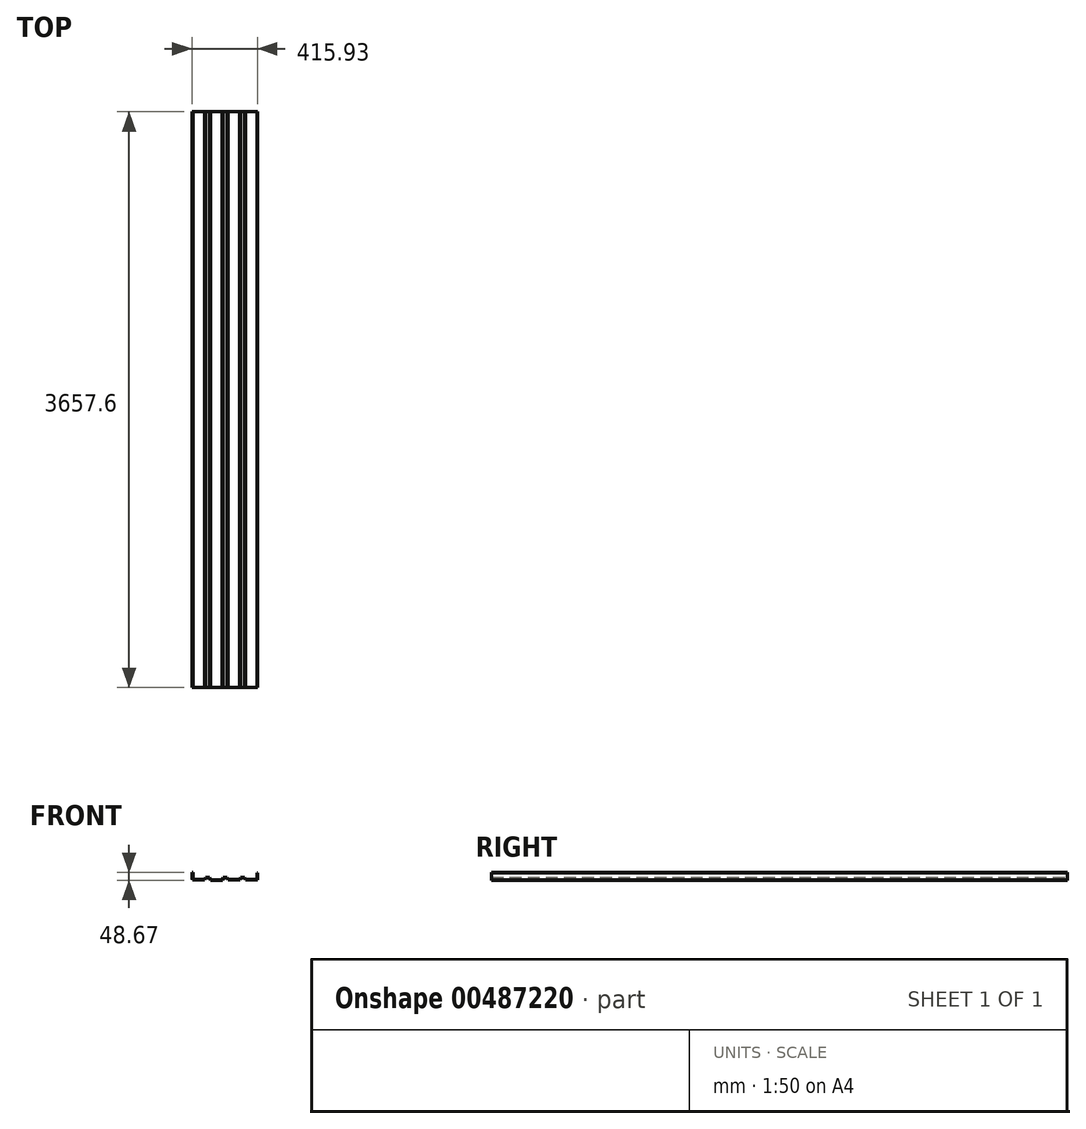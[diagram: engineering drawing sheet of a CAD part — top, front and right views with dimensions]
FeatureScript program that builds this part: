
annotation { "Feature Type Name" : "Feature", "Feature Type Description" : "" }
export const myFeature = defineFeature(function(context is Context, id is Id, definition is map)
    precondition{}
    {
        {
            var Q0;
            Q0=qCreatedBy(makeId("Front.planeOp"),FACE);
            var sketch = newSketch(context, id + "F0", { "sketchPlane" : qUnion([Q0])});
            skLineSegment(sketch, "E0.top", {"start": v(-11.38, 6.35) * mm, "end": v(14.02, 6.35) * mm});
            skPoint(sketch, "E0.middle", {"position": v(0, 0) * mm});
            skLineSegment(sketch, "E1.top", {"start": v(99.74, 6.35) * mm, "end": v(125.14, 6.35) * mm});
            skPoint(sketch, "E1.middle", {"position": v(111.12, 0) * mm});
            skLineSegment(sketch, "E2.top", {"start": v(-98.42, 6.35) * mm, "end": v(-123.83, 6.35) * mm});
            skPoint(sketch, "E2.middle", {"position": v(-111.12, 0) * mm});
            skLineSegment(sketch, "E3", {"start": v(-130.17, -6.35) * mm, "end": v(-123.83, 6.35) * mm});
            skLineSegment(sketch, "E4", {"start": v(-90.76, -8.98) * mm, "end": v(-98.42, 6.35) * mm});
            skLineSegment(sketch, "E5", {"start": v(-17.73, -8.98) * mm, "end": v(-11.38, 6.35) * mm});
            skLineSegment(sketch, "E6", {"start": v(20.37, -6.35) * mm, "end": v(14.02, 6.35) * mm});
            skLineSegment(sketch, "E7", {"start": v(93.4, -6.35) * mm, "end": v(99.74, 6.35) * mm});
            skLineSegment(sketch, "E8", {"start": v(131.5, -6.35) * mm, "end": v(125.14, 6.35) * mm});
            skLineSegment(sketch, "E9", {"start": v(-90.76, -8.98) * mm, "end": v(-17.73, -8.98) * mm});
            skLineSegment(sketch, "E10", {"start": v(20.37, -6.35) * mm, "end": v(93.4, -6.35) * mm});
            skLineSegment(sketch, "E11", {"start": v(131.5, -6.35) * mm, "end": v(203.2, -6.35) * mm});
            skLineSegment(sketch, "E12", {"start": v(-130.18, -6.35) * mm, "end": v(-203.2, -6.35) * mm});
            skLineSegment(sketch, "E13", {"start": v(-203.2, -6.35) * mm, "end": v(-203.2, 38.1) * mm});
            skLineSegment(sketch, "E14", {"start": v(-203.2, 38.1) * mm, "end": v(-209.55, 38.1) * mm});
            skLineSegment(sketch, "E15.0", {"start": v(-204.79, -7.94) * mm, "end": v(-204.79, 36.51) * mm});
            skLineSegment(sketch, "E15.1", {"start": v(-129.2, -7.94) * mm, "end": v(-204.79, -7.94) * mm});
            skLineSegment(sketch, "E15.2", {"start": v(-129.2, -7.94) * mm, "end": v(-122.84, 4.76) * mm});
            skLineSegment(sketch, "E15.3", {"start": v(-99.4, 4.76) * mm, "end": v(-122.84, 4.76) * mm});
            skLineSegment(sketch, "E15.4", {"start": v(94.37, -7.94) * mm, "end": v(100.72, 4.76) * mm});
            skLineSegment(sketch, "E15.5", {"start": v(100.72, 4.76) * mm, "end": v(124.16, 4.76) * mm});
            skLineSegment(sketch, "E15.6", {"start": v(130.51, -7.94) * mm, "end": v(124.16, 4.76) * mm});
            skLineSegment(sketch, "E15.7", {"start": v(130.51, -7.94) * mm, "end": v(204.52, -7.94) * mm});
            skLineSegment(sketch, "E15.8", {"start": v(19.39, -7.94) * mm, "end": v(94.37, -7.94) * mm});
            skLineSegment(sketch, "E15.9", {"start": v(19.39, -7.94) * mm, "end": v(13.04, 4.76) * mm});
            skLineSegment(sketch, "E15.10", {"start": v(-10.32, 4.76) * mm, "end": v(13.04, 4.76) * mm});
            skLineSegment(sketch, "E15.11", {"start": v(-16.67, -10.57) * mm, "end": v(-10.32, 4.76) * mm});
            skLineSegment(sketch, "E15.12", {"start": v(-91.74, -10.57) * mm, "end": v(-16.67, -10.57) * mm});
            skLineSegment(sketch, "E15.13", {"start": v(-91.74, -10.57) * mm, "end": v(-99.4, 4.76) * mm});
            skLineSegment(sketch, "E16.0", {"start": v(-204.79, 36.51) * mm, "end": v(-207.96, 36.51) * mm});
            skLineSegment(sketch, "E17", {"start": v(-209.55, 38.1) * mm, "end": v(-209.55, -6.35) * mm});
            skLineSegment(sketch, "E18", {"start": v(-209.55, -6.35) * mm, "end": v(-207.96, -6.35) * mm});
            skLineSegment(sketch, "E19", {"start": v(-207.96, -6.35) * mm, "end": v(-207.96, 36.51) * mm});
            skLineSegment(sketch, "E20", {"start": v(203.2, -6.35) * mm, "end": v(203.2, 36.51) * mm});
            skLineSegment(sketch, "E21", {"start": v(203.2, 36.51) * mm, "end": v(206.38, 36.51) * mm});
            skLineSegment(sketch, "E22", {"start": v(206.38, 36.51) * mm, "end": v(206.38, -7.94) * mm});
            skLineSegment(sketch, "E23", {"start": v(206.38, -7.94) * mm, "end": v(204.52, -7.94) * mm});
            skPoint(sketch, "E24.orphan", {"position": v(-203.2, 36.51) * mm});
            skSolve(sketch);
        }
        {
            var Q0;
            Q0 = qSketchRegion(id + "F0", true);
            extrude(context, id + "F1", {"entities" : qUnion([Q0]), "endBound" : BoundingType.SYMMETRIC, "depth" : 3657.6 * mm});
        }
    });
